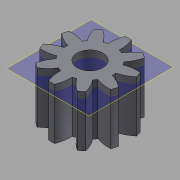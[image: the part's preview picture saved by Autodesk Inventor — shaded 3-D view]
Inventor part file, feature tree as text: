
AUTODESK INVENTOR PART (.ipt)
format: ipt  version: 2015 (Build 190159000, 159)  size: 167,936 bytes
history: native  units: in
note: dims shown in document units (in); Inventor stores cm internally (conversion verified against a paired STEP export)
features: other x13, sketch x3, plane x2
ambient origin geometry x8: Origin, YZ Plane, XZ Plane, XY Plane, X Axis, Y Axis, Z Axis, Center Point
bodies: Solid1 (feature_tree)
feature tree (18):
  other  "Spur Gear1"
  other  "Solid1::Spur Gear1"
  other  "TaggingFeature1"
  sketch  "Sketch1"  dims[d0=0.3937in]
  sketch  "Sketch2"  dims[d16=0.4528in d17=0.0in d41=0.0in d43=0.4528in d46=0.4528in d47=0.0in d48=0.0in]
  sketch  "Sketch3"
  plane  "XZ Plane_1"
  plane  "Work Plane2"
  other  "Z Axis_1"
  other  "Srf1"
  other  "Srf1::Derived"
  other  "Distance iMate"
  other  "Align iMate"
  other  "Mesh iMate"
  other  "Axis iMate"
  other  "Position iMate"
  other  "Mesh iMate2"
  other  "Start plane iMate"
